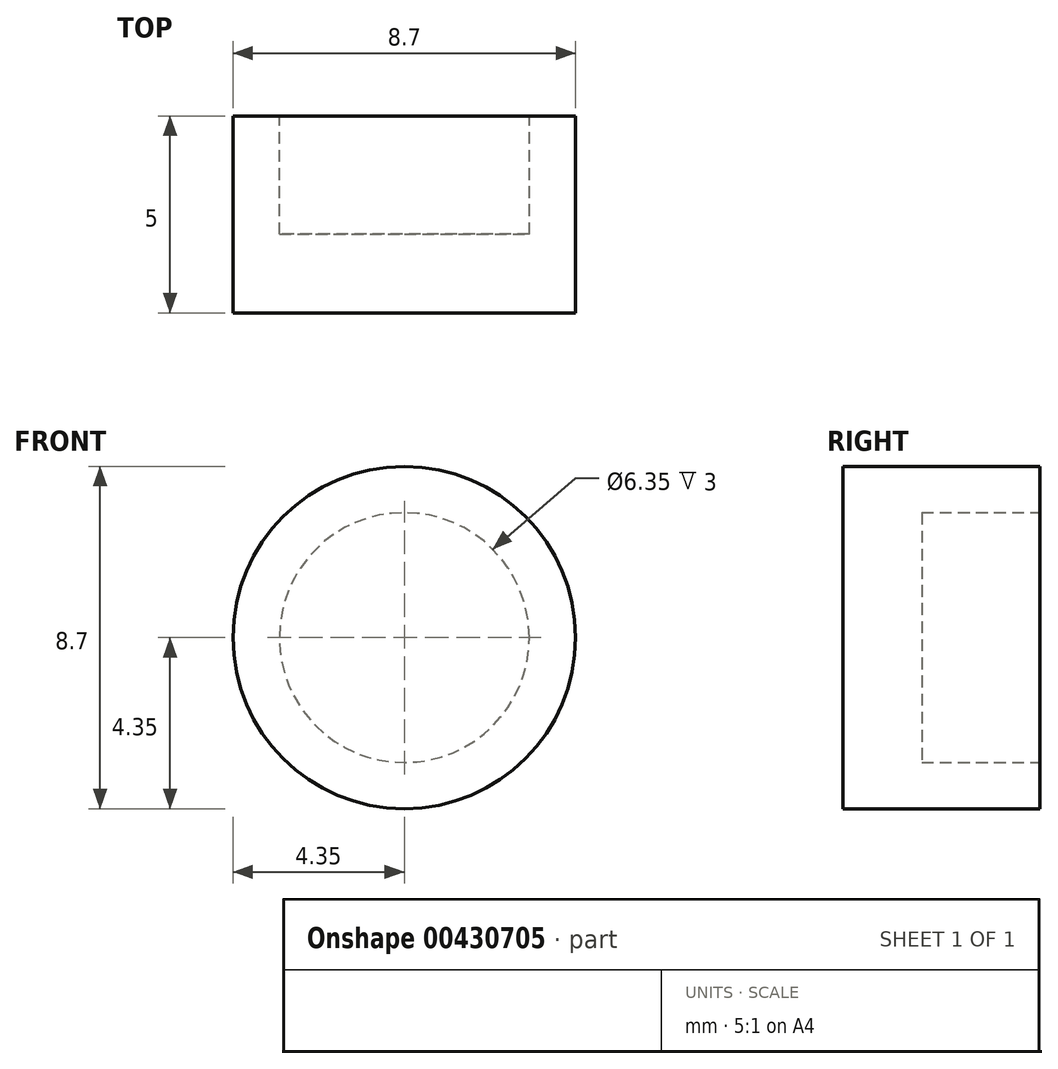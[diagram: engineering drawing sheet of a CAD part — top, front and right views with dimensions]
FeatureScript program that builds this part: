
annotation { "Feature Type Name" : "Feature", "Feature Type Description" : "" }
export const myFeature = defineFeature(function(context is Context, id is Id, definition is map)
    precondition{}
    {
        {
            var Q0;
            Q0=qCreatedBy(makeId("Front.planeOp"),FACE);
            var sketch = newSketch(context, id + "F0", { "sketchPlane" : qUnion([Q0])});
            skCircle(sketch, "E0", {"center": v(0, 0) * mm, "radius": 4.35 * mm});
            skSolve(sketch);
        }
        {
            var Q0;
            Q0 = qSketchRegion(id + "F0", true);
            extrude(context, id + "F1", {"entities" : qUnion([Q0]), "oppositeDirection" : true, "depth" : 5 * mm});
        }
        {
            var Q0;
            Q0=makeQuery(id+"F1.opExtrude","CAP_FACE",FACE,{"disambiguationData":[OSD([sQuery(id+"F0.wireOp",EDGE,"E0")])],"isStart":false});
            var sketch = newSketch(context, id + "F2", { "sketchPlane" : qUnion([Q0])});
            skCircle(sketch, "E1", {"center": v(0, 0) * mm, "radius": 3.17 * mm});
            skSolve(sketch);
        }
        {
            var Q0;
            Q0 = qSketchRegion(id + "F2", true);
            extrude(context, id + "F3", {"entities" : qUnion([Q0]), "operationType" : NewBodyOperationType.REMOVE, "oppositeDirection" : true, "depth" : 3 * mm});
        }
    });
